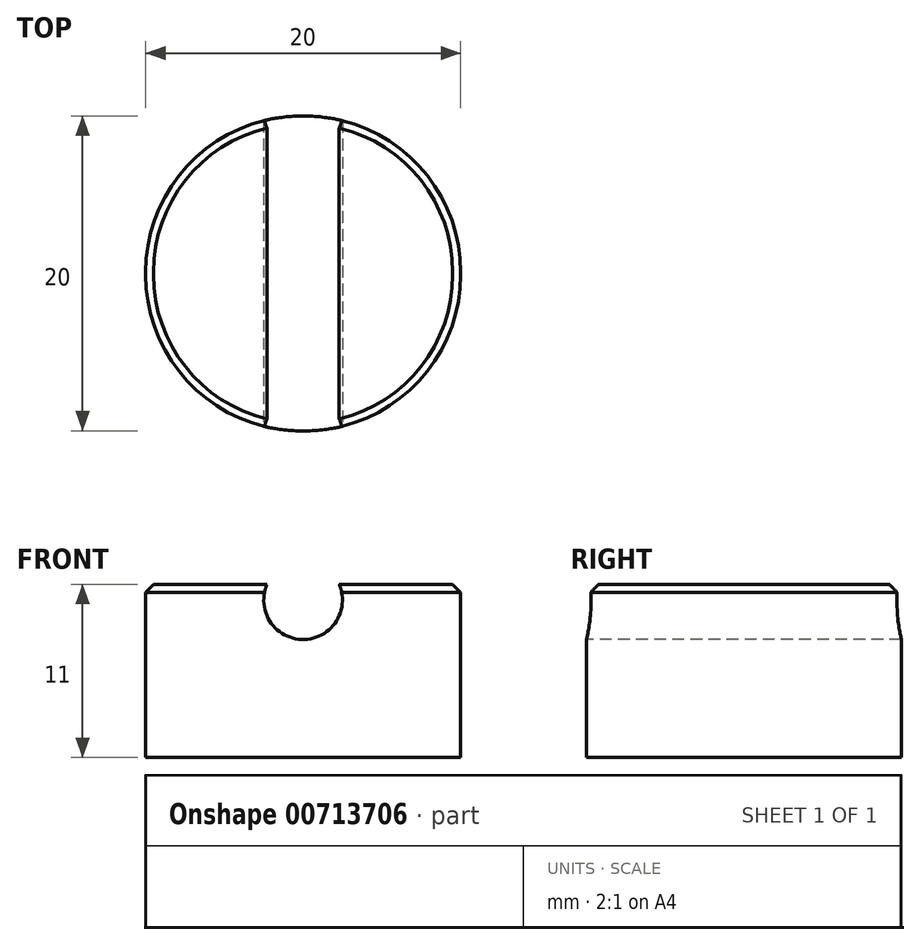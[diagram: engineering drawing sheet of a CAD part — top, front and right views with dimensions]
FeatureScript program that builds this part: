
annotation { "Feature Type Name" : "Feature", "Feature Type Description" : "" }
export const myFeature = defineFeature(function(context is Context, id is Id, definition is map)
    precondition{}
    {
        {
            var Q0;
            Q0=qCreatedBy(makeId("Top.planeOp"),FACE);
            var sketch = newSketch(context, id + "F0", { "sketchPlane" : qUnion([Q0])});
            skLineSegment(sketch, "E0.bottom", {"start": v(-3.27, 10.95) * mm, "end": v(-3.07, 10.95) * mm});
            skLineSegment(sketch, "E0.top", {"start": v(-3.27, -9.05) * mm, "end": v(-3.07, -9.05) * mm});
            skLineSegment(sketch, "E0.left", {"start": v(-13.17, 1.05) * mm, "end": v(-13.17, 0.85) * mm});
            skLineSegment(sketch, "E0.right", {"start": v(6.83, 1.05) * mm, "end": v(6.83, 0.85) * mm});
            skPoint(sketch, "E1.visualSharp", {"position": v(-13.17, -9.05) * mm});
            skArc(sketch, "E1.filletArc", {"start": v(-13.17, 0.85) * mm, "mid": v(-10.27, -6.15) * mm, "end": v(-3.27, -9.05) * mm});
            skPoint(sketch, "E2.visualSharp", {"position": v(6.83, -9.05) * mm});
            skArc(sketch, "E2.filletArc", {"start": v(-3.07, -9.05) * mm, "mid": v(3.93, -6.15) * mm, "end": v(6.83, 0.85) * mm});
            skPoint(sketch, "E3.visualSharp", {"position": v(-13.17, 10.95) * mm});
            skArc(sketch, "E3.filletArc", {"start": v(-3.27, 10.95) * mm, "mid": v(-10.27, 8.05) * mm, "end": v(-13.17, 1.05) * mm});
            skPoint(sketch, "E4.visualSharp", {"position": v(6.83, 10.95) * mm});
            skArc(sketch, "E4.filletArc", {"start": v(6.83, 1.05) * mm, "mid": v(3.93, 8.05) * mm, "end": v(-3.07, 10.95) * mm});
            skSolve(sketch);
        }
        {
            var Q0;
            Q0 = qSketchRegion(id + "F0", true);
            extrude(context, id + "F1", {"entities" : qUnion([Q0]), "depth" : 6 * mm, "offsetDistance" : 25 * mm});
        }
        {
            var Q0;
            Q0=makeQuery(id+"F1.opExtrude","SWEPT_FACE",FACE,{"disambiguationData":[OSD([sQuery(id+"F0.wireOp",EDGE,"E0.top")])]});
            var sketch = newSketch(context, id + "F2", { "sketchPlane" : qUnion([Q0])});
            skCircle(sketch, "E5", {"center": v(-3.17, 5) * mm, "radius": 2.5 * mm});
            skSolve(sketch);
        }
        {
            var Q0;
            Q0 = qSketchRegion(id + "F2", true);
            extrude(context, id + "F3", {"entities" : qUnion([Q0]), "operationType" : NewBodyOperationType.REMOVE, "oppositeDirection" : true, "depth" : 25 * mm, "offsetDistance" : 25 * mm});
        }
        {
            var Q0;
            Q0=makeQuery(id+"F1.opExtrude","CAP_EDGE",EDGE,{"disambiguationData":[OSD([sQuery(id+"F0.wireOp",EDGE,"E4.filletArc")])],"isStart":false});
            var Q1;
            Q1=makeQuery(id+"F1.opExtrude","CAP_EDGE",EDGE,{"disambiguationData":[OSD([sQuery(id+"F0.wireOp",EDGE,"E3.filletArc")])],"isStart":false});
            chamfer(context, id + "F4", {"entities" : qUnion([Q0, Q1]), "width" : 0.5 * mm, "tangentPropagation" : true});
        }
        {
            var Q0;
            Q0=makeQuery(id+"F1.opExtrude","CAP_FACE",FACE,{"disambiguationData":[OSD([sQuery(id+"F0.wireOp",EDGE,"E0.bottom"),sQuery(id+"F0.wireOp",EDGE,"E0.top"),sQuery(id+"F0.wireOp",EDGE,"E0.left"),sQuery(id+"F0.wireOp",EDGE,"E0.right"),sQuery(id+"F0.wireOp",EDGE,"E1.filletArc"),sQuery(id+"F0.wireOp",EDGE,"E2.filletArc"),sQuery(id+"F0.wireOp",EDGE,"E3.filletArc"),sQuery(id+"F0.wireOp",EDGE,"E4.filletArc")])],"isStart":true});
            extrude(context, id + "F5", {"entities" : qUnion([Q0]), "operationType" : NewBodyOperationType.ADD, "depth" : 5 * mm, "offsetDistance" : 25 * mm});
        }
    });
